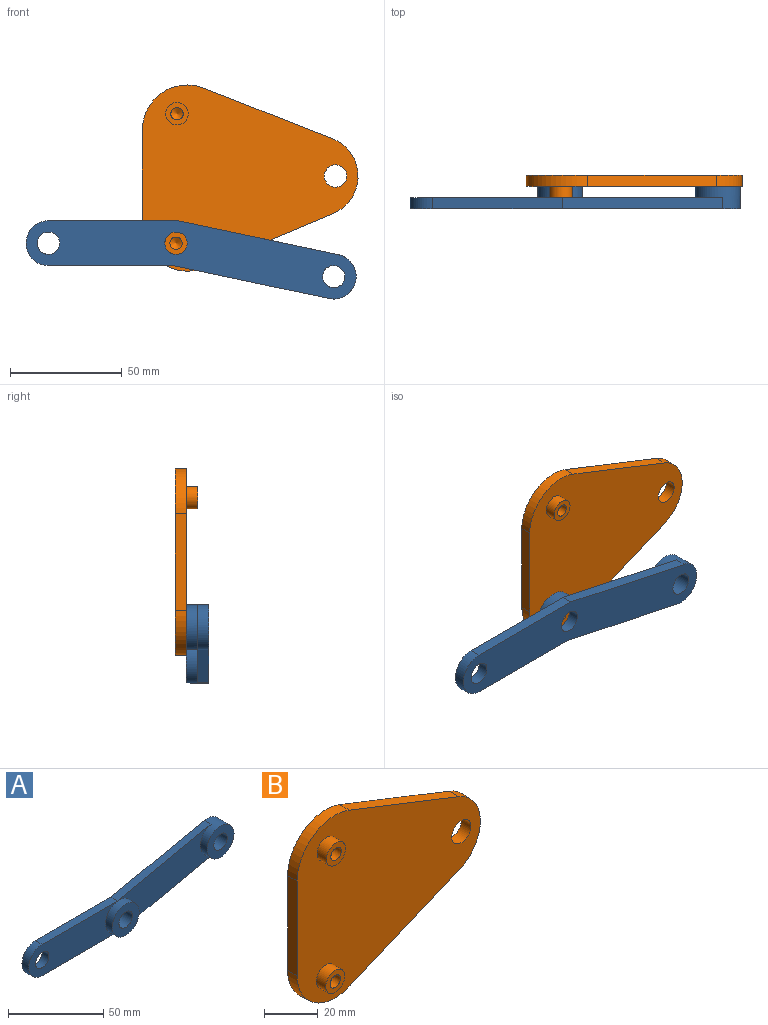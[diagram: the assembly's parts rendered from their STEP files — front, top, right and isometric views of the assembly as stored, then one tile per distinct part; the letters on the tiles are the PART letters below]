
ASSEMBLY  parts=2 mates=1
PART A: 15 faces, bbox 147.4x10x34.9 mm
  f0: plane 2.07x0.22mm, normal (0,-1,0), area 0mm2, adj f2,f3,f12
  f1: plane 69.41x14.71mm, normal (-0.21,0,0.98), area 354.8mm2, adj f4,f5,f6,f10
  f2: plane 71.46x15.15mm, normal (0.21,0,-0.98), area 365.2mm2, adj f0,f3,f4,f6,f10
  f3: plane 58.05x5mm, normal (0,0,-1), area 290.2mm2, adj f0,f2,f4,f6,f11
  f4: plane 139.51x34.71mm, normal (0,-1,0), area 2187.3mm2, adj f1,f2,f3,f5,f9,f10,f11,f12
  f5: plane 55.95x5mm, normal (0,0,1), area 279.8mm2, adj f1,f4,f6,f11
  f6: plane 147.43x34.93mm, normal (0,1,0), area 2658.5mm2, adj f1,f2,f3,f5,f7,f8,f9,f10
  f7: cylinder r=5mm len=10mm, axis (0,-1,0), area 314.2mm2, adj f6,f13
  f8: cylinder r=5mm len=10mm, axis (0,-1,0), area 314.2mm2, adj f6,f14
  f9: cylinder r=5mm len=10mm, axis (0,-1,0), area 157.1mm2, adj f4,f6
  f10: cylinder r=10mm len=20mm, axis (0,-1,0), area 471.2mm2, adj f1,f2,f4,f6,f14
  f11: cylinder r=10mm len=20mm, axis (0,1,0), area 157.1mm2, adj f3,f4,f5,f6
  f12: cylinder r=10mm len=20mm, axis (0,1,0), area 314.2mm2, adj f0,f4,f13
  f13: plane 20x20mm, normal (0,-1,0), area 235.6mm2, adj f7,f12
  f14: plane 20x20mm, normal (0,-1,0), area 235.6mm2, adj f8,f10
PART B: 17 faces, bbox 96.3x10x83.1 mm
  f0: plane 43.13x5mm, normal (-1,0,0), area 215.7mm2, adj f4,f5,f6,f8
  f1: plane 57.51x24.22mm, normal (0.39,0,-0.92), area 312mm2, adj f4,f5,f7,f8
  f2: cylinder r=5mm len=10mm, axis (0,1,0), area 157.1mm2, adj f4,f5
  f3: plane 57.55x22.62mm, normal (0.37,0,0.93), area 309.2mm2, adj f4,f5,f6,f7
  f4: plane 96.28x83.13mm, normal (0,-1,0), area 5411mm2, adj f0,f1,f2,f3,f6,f7,f8,f9
  f5: plane 96.28x83.13mm, normal (0,1,0), area 5568.1mm2, adj f0,f1,f2,f3,f6,f7,f8
  f6: cylinder r=20mm len=27.32mm, axis (0,-1,0), area 194.5mm2, adj f0,f3,f4,f5
  f7: cylinder r=18mm len=33.34mm, axis (0,1,0), area 213.2mm2, adj f1,f3,f4,f5
  f8: cylinder r=20mm len=27.76mm, axis (0,-1,0), area 196.9mm2, adj f0,f1,f4,f5
  f9: cylinder r=5mm len=10mm, axis (0,1,0), area 157.1mm2, adj f4,f10
  f10: plane 10x10mm, normal (0,-1,0), area 54.8mm2, adj f9,f13
  f11: cylinder r=5mm len=10mm, axis (0,1,0), area 157.1mm2, adj f4,f12
  f12: plane 10x10mm, normal (0,-1,0), area 54.8mm2, adj f11,f15
  f13: cylinder r=2.75mm len=5.5mm, axis (0,-1,0), area 86.4mm2, adj f10,f14
  f14: cone r=0mm half-angle=59deg, axis (0,-1,0), area 27.7mm2, adj f13
  f15: cylinder r=2.75mm len=5.5mm, axis (0,-1,0), area 86.4mm2, adj f12,f16
  f16: cone r=0mm half-angle=59deg, axis (0,-1,0), area 27.7mm2, adj f15
PLACE A rot(axis=(-1,0,0),180deg) t=(15,-12.5,20)mm
PLACE B at identity fixed
MATE revolute A.f12 <-> B.f11  axis (0,1,0) through (15,-5,20)mm
